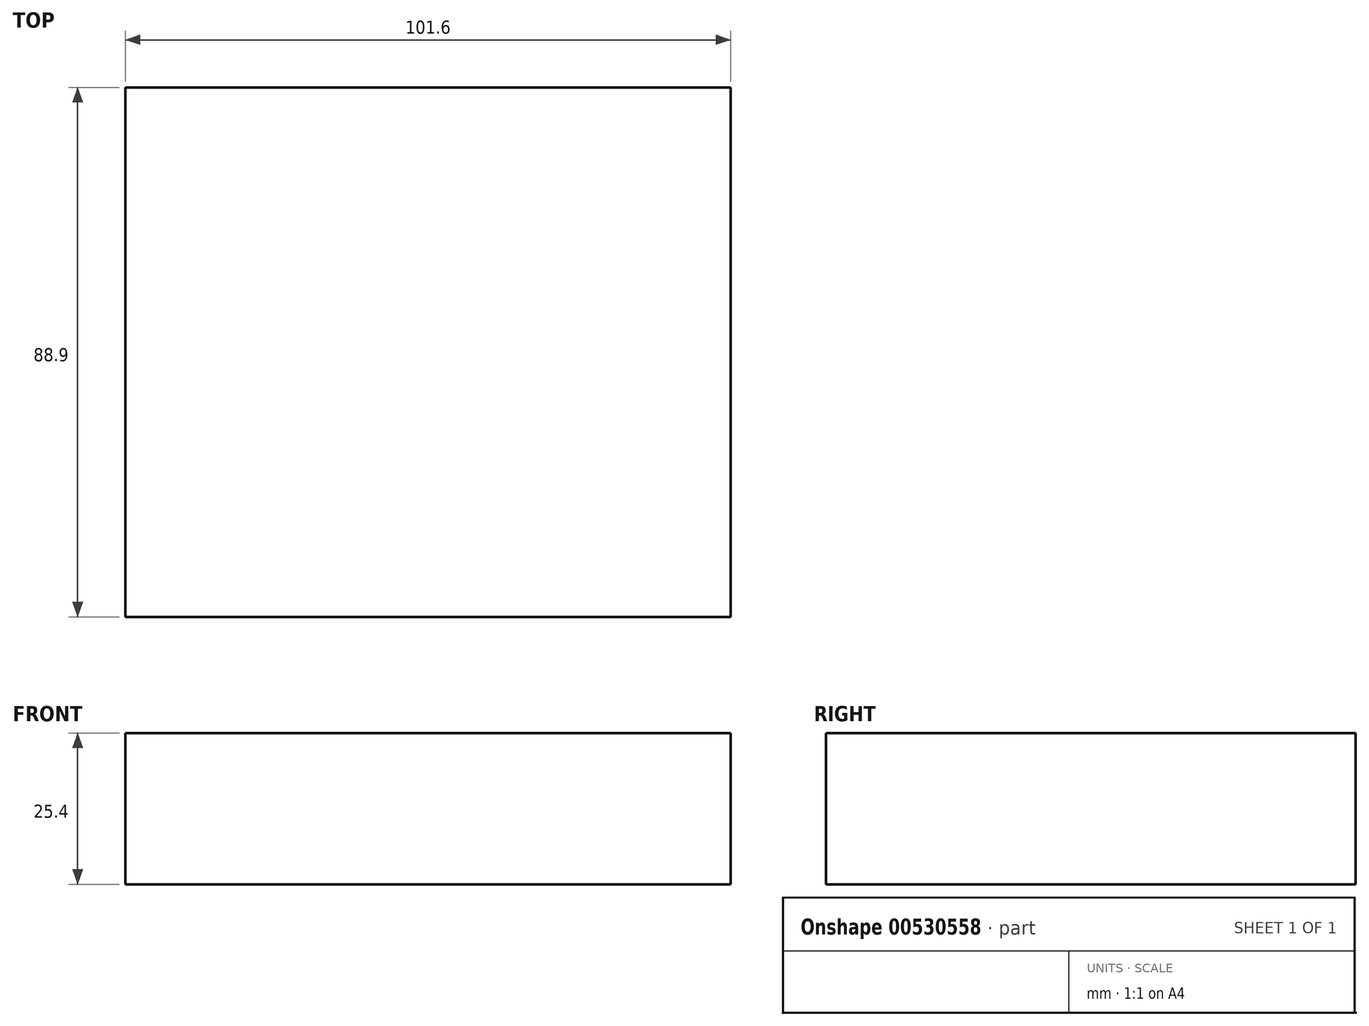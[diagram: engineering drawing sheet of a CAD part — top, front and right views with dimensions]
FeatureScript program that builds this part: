
annotation { "Feature Type Name" : "Feature", "Feature Type Description" : "" }
export const myFeature = defineFeature(function(context is Context, id is Id, definition is map)
    precondition{}
    {
        {
            var Q0;
            Q0=qCreatedBy(makeId("Top.planeOp"),FACE);
            var sketch = newSketch(context, id + "F0", { "sketchPlane" : qUnion([Q0])});
            skLineSegment(sketch, "E0.bottom", {"start": v(0, 0) * mm, "end": v(101.6, 0) * mm});
            skLineSegment(sketch, "E0.top", {"start": v(0, -88.9) * mm, "end": v(101.6, -88.9) * mm});
            skLineSegment(sketch, "E0.left", {"start": v(0, 0) * mm, "end": v(0, -88.9) * mm});
            skLineSegment(sketch, "E0.right", {"start": v(101.6, 0) * mm, "end": v(101.6, -88.9) * mm});
            skSolve(sketch);
        }
        {
            var Q0;
            Q0 = qSketchRegion(id + "F0", true);
            extrude(context, id + "F1", {"entities" : qUnion([Q0]), "depth" : 25.4 * mm, "offsetDistance" : 25.4 * mm});
        }
    });
